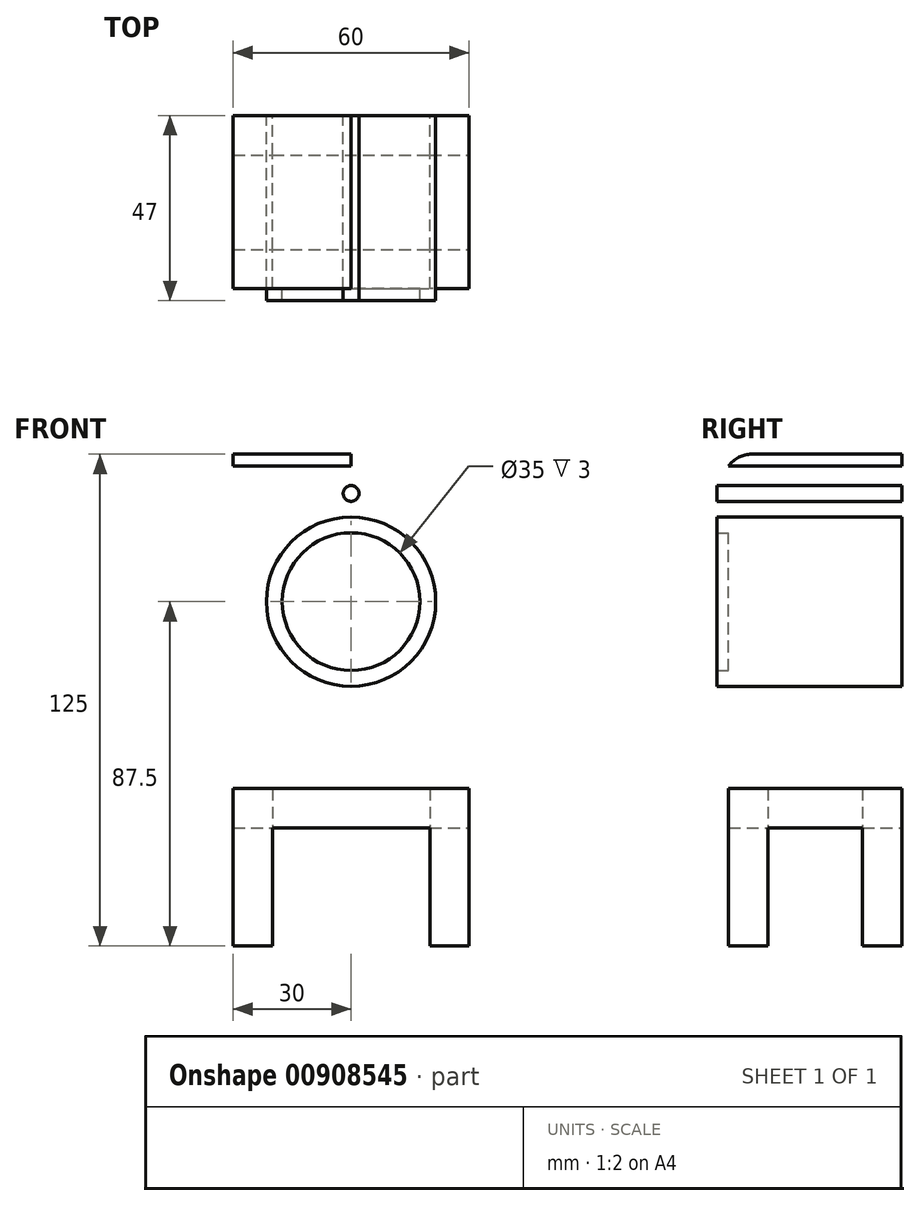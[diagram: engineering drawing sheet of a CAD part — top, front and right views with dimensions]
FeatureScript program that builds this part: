
annotation { "Feature Type Name" : "Feature", "Feature Type Description" : "" }
export const myFeature = defineFeature(function(context is Context, id is Id, definition is map)
    precondition{}
    {
        {
            var Q0;
            Q0=qCreatedBy(makeId("Front.planeOp"),FACE);
            var sketch = newSketch(context, id + "F0", { "sketchPlane" : qUnion([Q0])});
            skLineSegment(sketch, "E0.bottom", {"start": v(-30, 42.5) * mm, "end": v(30, 42.5) * mm});
            skLineSegment(sketch, "E0.top", {"start": v(-30, -42.5) * mm, "end": v(30, -42.5) * mm});
            skLineSegment(sketch, "E0.left", {"start": v(-30, 42.5) * mm, "end": v(-30, -42.5) * mm});
            skLineSegment(sketch, "E0.right", {"start": v(30, 42.5) * mm, "end": v(30, -42.5) * mm});
            skPoint(sketch, "E0.middle", {"position": v(0, 0) * mm});
            skPoint(sketch, "E1", {"position": v(0, 26.5) * mm});
            skPoint(sketch, "E1.positionSnap0", {"position": v(0, 42.5) * mm});
            skLineSegment(sketch, "E2", {"start": v(0, 42.5) * mm, "end": v(0, 26.5) * mm});
            skPoint(sketch, "E3", {"position": v(0, -16.5) * mm});
            skLineSegment(sketch, "E4", {"start": v(0, 26.5) * mm, "end": v(0, -16.5) * mm});
            skPoint(sketch, "E5", {"position": v(0, 5) * mm});
            skCircle(sketch, "E6", {"center": v(0, 5) * mm, "radius": 21.5 * mm});
            skCircle(sketch, "E7.0", {"center": v(0, 5) * mm, "radius": 17.5 * mm});
            skLineSegment(sketch, "E8.top", {"start": v(-30, 27.5) * mm, "end": v(30, 27.5) * mm});
            skLineSegment(sketch, "E8.left", {"start": v(-30, 42.5) * mm, "end": v(-30, 27.5) * mm});
            skLineSegment(sketch, "E8.right", {"start": v(30, 42.5) * mm, "end": v(30, 27.5) * mm});
            skLineSegment(sketch, "E9.top", {"start": v(-30, 39.5) * mm, "end": v(30, 39.5) * mm});
            skLineSegment(sketch, "E9.left", {"start": v(-30, 42.5) * mm, "end": v(-30, 39.5) * mm});
            skLineSegment(sketch, "E9.right", {"start": v(30, 42.5) * mm, "end": v(30, 39.5) * mm});
            skPoint(sketch, "E10", {"position": v(0, 32.5) * mm});
            skCircle(sketch, "E11", {"center": v(0, 32.5) * mm, "radius": 2 * mm});
            skLineSegment(sketch, "E12.bottom", {"start": v(-30, -42.5) * mm, "end": v(-20, -42.5) * mm});
            skLineSegment(sketch, "E12.top", {"start": v(-30, -82.5) * mm, "end": v(-20, -82.5) * mm});
            skLineSegment(sketch, "E12.left", {"start": v(-30, -42.5) * mm, "end": v(-30, -82.5) * mm});
            skLineSegment(sketch, "E12.right", {"start": v(-20, -42.5) * mm, "end": v(-20, -82.5) * mm});
            skLineSegment(sketch, "E13.bottom", {"start": v(30, -42.5) * mm, "end": v(20, -42.5) * mm});
            skLineSegment(sketch, "E13.top", {"start": v(30, -82.5) * mm, "end": v(20, -82.5) * mm});
            skLineSegment(sketch, "E13.left", {"start": v(30, -42.5) * mm, "end": v(30, -82.5) * mm});
            skLineSegment(sketch, "E13.right", {"start": v(20, -42.5) * mm, "end": v(20, -82.5) * mm});
            skLineSegment(sketch, "E14.top", {"start": v(-30, -52.5) * mm, "end": v(30, -52.5) * mm});
            skLineSegment(sketch, "E14.left", {"start": v(-30, -42.5) * mm, "end": v(-30, -52.5) * mm});
            skLineSegment(sketch, "E14.right", {"start": v(30, -42.5) * mm, "end": v(30, -52.5) * mm});
            skLineSegment(sketch, "E15.top", {"start": v(-30, -82.5) * mm, "end": v(30, -82.5) * mm});
            skSolve(sketch);
        }
        {
            var Q0;
            {var subQ0=sQuery(id+"F0.wireOp",EDGE,"E6");var subQ1=sQuery(id+"F0.wireOp",EDGE,"E4");var subQ2=makeQuery(id+"F0.imprint","INTERSECT",VERTEX,{"disambiguationData":[OD(0.0)],"derivedFrom":[subQ1,subQ0]});Q0=makeQuery(id+"F0.imprint","IMPRINT",FACE,{"disambiguationData":[TD([[makeQuery(id+"F0.imprint","IMPRINT",EDGE,{"disambiguationData":[TD([[subQ2,-1.0]])],"derivedFrom":subQ1}),-1.0]])]});}
            var Q1;
            {var subQ0=sQuery(id+"F0.wireOp",EDGE,"E6");var subQ1=sQuery(id+"F0.wireOp",EDGE,"E4");var subQ2=makeQuery(id+"F0.imprint","INTERSECT",VERTEX,{"disambiguationData":[OD(0.0)],"derivedFrom":[subQ1,subQ0]});Q1=makeQuery(id+"F0.imprint","IMPRINT",FACE,{"disambiguationData":[TD([[makeQuery(id+"F0.imprint","IMPRINT",EDGE,{"disambiguationData":[TD([[subQ2,-1.0]])],"derivedFrom":subQ1}),1.0]])]});}
            var Q2;
            {var subQ0=sQuery(id+"F0.wireOp",EDGE,"E8.left");Q2=makeQuery(id+"F0.imprint","IMPRINT",FACE,{"disambiguationData":[TD([[makeQuery(id+"F0.imprint","IMPRINT",EDGE,{"derivedFrom":subQ0}),1.0]])]});}
            var Q3;
            {var subQ0=sQuery(id+"F0.wireOp",EDGE,"E8.right");Q3=makeQuery(id+"F0.imprint","IMPRINT",FACE,{"disambiguationData":[TD([[makeQuery(id+"F0.imprint","IMPRINT",EDGE,{"derivedFrom":subQ0}),-1.0]])]});}
            var Q4;
            {var subQ5=sQuery(id+"F0.wireOp",EDGE,"E9.right");Q4=makeQuery(id+"F0.imprint","IMPRINT",FACE,{"disambiguationData":[TD([[makeQuery(id+"F0.imprint","IMPRINT",EDGE,{"derivedFrom":subQ5}),-1.0]])]});}
            var Q5;
            {var subQ5=sQuery(id+"F0.wireOp",EDGE,"E9.left");Q5=makeQuery(id+"F0.imprint","IMPRINT",FACE,{"disambiguationData":[TD([[makeQuery(id+"F0.imprint","IMPRINT",EDGE,{"derivedFrom":subQ5}),1.0]])]});}
            var Q6;
            {var subQ0=sQuery(id+"F0.wireOp",EDGE,"E7.0");var subQ1=sQuery(id+"F0.wireOp",EDGE,"E4");var subQ2=makeQuery(id+"F0.imprint","INTERSECT",VERTEX,{"disambiguationData":[OD(0.0)],"derivedFrom":[subQ1,subQ0]});Q6=makeQuery(id+"F0.imprint","IMPRINT",FACE,{"disambiguationData":[TD([[makeQuery(id+"F0.imprint","IMPRINT",EDGE,{"disambiguationData":[TD([[subQ2,-1.0]])],"derivedFrom":subQ1}),1.0]])]});}
            var Q7;
            {var subQ0=sQuery(id+"F0.wireOp",EDGE,"E7.0");var subQ1=sQuery(id+"F0.wireOp",EDGE,"E4");var subQ2=makeQuery(id+"F0.imprint","INTERSECT",VERTEX,{"disambiguationData":[OD(0.0)],"derivedFrom":[subQ1,subQ0]});Q7=makeQuery(id+"F0.imprint","IMPRINT",FACE,{"disambiguationData":[TD([[makeQuery(id+"F0.imprint","IMPRINT",EDGE,{"disambiguationData":[TD([[subQ2,-1.0]])],"derivedFrom":subQ1}),-1.0]])]});}
            var Q8;
            {var subQ7=sQuery(id+"F0.wireOp",EDGE,"E0.left");Q8=makeQuery(id+"F0.imprint","IMPRINT",FACE,{"disambiguationData":[TD([[makeQuery(id+"F0.imprint","IMPRINT",EDGE,{"derivedFrom":subQ7}),1.0]])]});}
            var Q9;
            {var subQ0=sQuery(id+"F0.wireOp",EDGE,"E15.top");var subQ1=sQuery(id+"F0.wireOp",EDGE,"E13.right");var subQ2=makeQuery(id+"F0.imprint","INTERSECT",VERTEX,{"derivedFrom":[subQ1,subQ0]});Q9=makeQuery(id+"F0.imprint","IMPRINT",FACE,{"disambiguationData":[TD([[makeQuery(id+"F0.imprint","IMPRINT",EDGE,{"disambiguationData":[TD([[subQ2,1.0]])],"derivedFrom":subQ1}),1.0]])]});}
            var Q10;
            {var subQ0=sQuery(id+"F0.wireOp",EDGE,"E0.top");var subQ1=sQuery(id+"F0.wireOp",EDGE,"E13.right");var subQ2=makeQuery(id+"F0.imprint","INTERSECT",VERTEX,{"derivedFrom":[subQ1,subQ0]});Q10=makeQuery(id+"F0.imprint","IMPRINT",FACE,{"disambiguationData":[TD([[makeQuery(id+"F0.imprint","IMPRINT",EDGE,{"disambiguationData":[TD([[subQ2,-1.0]])],"derivedFrom":subQ1}),1.0]])]});}
            var Q11;
            {var subQ0=sQuery(id+"F0.wireOp",EDGE,"E0.top");var subQ1=sQuery(id+"F0.wireOp",EDGE,"E12.right");var subQ2=makeQuery(id+"F0.imprint","INTERSECT",VERTEX,{"derivedFrom":[subQ1,subQ0]});Q11=makeQuery(id+"F0.imprint","IMPRINT",FACE,{"disambiguationData":[TD([[makeQuery(id+"F0.imprint","IMPRINT",EDGE,{"disambiguationData":[TD([[subQ2,-1.0]])],"derivedFrom":subQ1}),-1.0]])]});}
            var Q12;
            {var subQ0=sQuery(id+"F0.wireOp",EDGE,"E15.top");var subQ1=sQuery(id+"F0.wireOp",EDGE,"E12.right");var subQ2=makeQuery(id+"F0.imprint","INTERSECT",VERTEX,{"derivedFrom":[subQ1,subQ0]});Q12=makeQuery(id+"F0.imprint","IMPRINT",FACE,{"disambiguationData":[TD([[makeQuery(id+"F0.imprint","IMPRINT",EDGE,{"disambiguationData":[TD([[subQ2,1.0]])],"derivedFrom":subQ1}),-1.0]])]});}
            var Q13;
            {var subQ0=sQuery(id+"F0.wireOp",EDGE,"E0.top");var subQ1=sQuery(id+"F0.wireOp",EDGE,"E12.right");var subQ2=makeQuery(id+"F0.imprint","INTERSECT",VERTEX,{"derivedFrom":[subQ1,subQ0]});Q13=makeQuery(id+"F0.imprint","IMPRINT",FACE,{"disambiguationData":[TD([[makeQuery(id+"F0.imprint","IMPRINT",EDGE,{"disambiguationData":[TD([[subQ2,-1.0]])],"derivedFrom":subQ1}),1.0]])]});}
            extrude(context, id + "F1", {"entities" : qUnion([Q0, Q1, Q2, Q3, Q4, Q5, Q6, Q7, Q8, Q9, Q10, Q11, Q12, Q13]), "depth" : 44 * mm, "offsetDistance" : 25 * mm});
        }
        {
            var Q0;
            {var subQ0=sQuery(id+"F0.wireOp",EDGE,"E6");var subQ1=sQuery(id+"F0.wireOp",EDGE,"E4");var subQ2=makeQuery(id+"F0.imprint","INTERSECT",VERTEX,{"disambiguationData":[OD(0.0)],"derivedFrom":[subQ1,subQ0]});Q0=makeQuery(id+"F0.imprint","IMPRINT",FACE,{"disambiguationData":[TD([[makeQuery(id+"F0.imprint","IMPRINT",EDGE,{"disambiguationData":[TD([[subQ2,-1.0]])],"derivedFrom":subQ1}),1.0]])]});}
            var Q1;
            {var subQ0=sQuery(id+"F0.wireOp",EDGE,"E6");var subQ1=sQuery(id+"F0.wireOp",EDGE,"E4");var subQ2=makeQuery(id+"F0.imprint","INTERSECT",VERTEX,{"disambiguationData":[OD(0.0)],"derivedFrom":[subQ1,subQ0]});Q1=makeQuery(id+"F0.imprint","IMPRINT",FACE,{"disambiguationData":[TD([[makeQuery(id+"F0.imprint","IMPRINT",EDGE,{"disambiguationData":[TD([[subQ2,-1.0]])],"derivedFrom":subQ1}),-1.0]])]});}
            var Q2;
            {var subQ0=sQuery(id+"F0.wireOp",EDGE,"zrFD8z1w-E58j-qKlx-5lVt-mCnEbS1Ubnud");var subQ1=sQuery(id+"F0.wireOp",EDGE,"E2");var subQ2=makeQuery(id+"F0.imprint","INTERSECT",VERTEX,{"disambiguationData":[OD(0.0)],"derivedFrom":[subQ1,subQ0]});Q2=makeQuery(id+"F0.imprint","IMPRINT",FACE,{"disambiguationData":[TD([[makeQuery(id+"F0.imprint","IMPRINT",EDGE,{"disambiguationData":[TD([[subQ2,-1.0]])],"derivedFrom":subQ1}),1.0]])]});}
            var Q3;
            {var subQ0=sQuery(id+"F0.wireOp",EDGE,"zrFD8z1w-E58j-qKlx-5lVt-mCnEbS1Ubnud");var subQ1=sQuery(id+"F0.wireOp",EDGE,"E2");var subQ2=makeQuery(id+"F0.imprint","INTERSECT",VERTEX,{"disambiguationData":[OD(0.0)],"derivedFrom":[subQ1,subQ0]});Q3=makeQuery(id+"F0.imprint","IMPRINT",FACE,{"disambiguationData":[TD([[makeQuery(id+"F0.imprint","IMPRINT",EDGE,{"disambiguationData":[TD([[subQ2,-1.0]])],"derivedFrom":subQ1}),-1.0]])]});}
            extrude(context, id + "F2", {"entities" : qUnion([Q0, Q1, Q2, Q3]), "operationType" : NewBodyOperationType.ADD, "depth" : 47 * mm, "offsetDistance" : 25 * mm});
        }
        {
            var Q0;
            Q0=makeQuery(id+"F1.opExtrude","CAP_EDGE",EDGE,{"disambiguationData":[OSD([sQuery(id+"F0.wireOp",EDGE,"E0.bottom")])],"isStart":false});
            fillet(context, id + "F3", {"entities" : qUnion([Q0]), "radius" : 7.24 * mm, "tangentPropagation" : true, "allowEdgeOverflow" : false});
        }
        {
            var Q0;
            {var subQ0=sQuery(id+"F0.wireOp",EDGE,"E15.top");var subQ1=sQuery(id+"F0.wireOp",EDGE,"E12.right");var subQ2=makeQuery(id+"F0.imprint","INTERSECT",VERTEX,{"derivedFrom":[subQ1,subQ0]});Q0=makeQuery(id+"F0.imprint","IMPRINT",FACE,{"disambiguationData":[TD([[makeQuery(id+"F0.imprint","IMPRINT",EDGE,{"disambiguationData":[TD([[subQ2,1.0]])],"derivedFrom":subQ1}),1.0]])]});}
            var Q1;
            {var subQ0=sQuery(id+"F0.wireOp",EDGE,"E15.top");var subQ1=sQuery(id+"F0.wireOp",EDGE,"E13.right");var subQ2=makeQuery(id+"F0.imprint","INTERSECT",VERTEX,{"derivedFrom":[subQ1,subQ0]});Q1=makeQuery(id+"F0.imprint","IMPRINT",FACE,{"disambiguationData":[TD([[makeQuery(id+"F0.imprint","IMPRINT",EDGE,{"disambiguationData":[TD([[subQ2,1.0]])],"derivedFrom":subQ1}),1.0]])]});}
            var Q2;
            {var subQ0=sQuery(id+"F0.wireOp",EDGE,"E15.top");var subQ1=sQuery(id+"F0.wireOp",EDGE,"E12.right");var subQ2=makeQuery(id+"F0.imprint","INTERSECT",VERTEX,{"derivedFrom":[subQ1,subQ0]});Q2=makeQuery(id+"F0.imprint","IMPRINT",FACE,{"disambiguationData":[TD([[makeQuery(id+"F0.imprint","IMPRINT",EDGE,{"disambiguationData":[TD([[subQ2,1.0]])],"derivedFrom":subQ1}),-1.0]])]});}
            var Q3;
            {var subQ0=sQuery(id+"F0.wireOp",EDGE,"E0.top");var subQ1=sQuery(id+"F0.wireOp",EDGE,"E12.right");var subQ2=makeQuery(id+"F0.imprint","INTERSECT",VERTEX,{"derivedFrom":[subQ1,subQ0]});Q3=makeQuery(id+"F0.imprint","IMPRINT",FACE,{"disambiguationData":[TD([[makeQuery(id+"F0.imprint","IMPRINT",EDGE,{"disambiguationData":[TD([[subQ2,-1.0]])],"derivedFrom":subQ1}),1.0]])]});}
            var Q4;
            {var subQ0=sQuery(id+"F0.wireOp",EDGE,"E12.top");var subQ1=sQuery(id+"F0.wireOp",EDGE,"E0.bottom");var subQ2=sQuery(id+"F0.wireOp",EDGE,"E14.right");var subQ3=sQuery(id+"F0.wireOp",EDGE,"E13.left");var subQ4=sQuery(id+"F0.wireOp",EDGE,"E9.right");var subQ5=sQuery(id+"F0.wireOp",EDGE,"E8.right");var subQ6=sQuery(id+"F0.wireOp",EDGE,"E0.right");var subQ7=sQuery(id+"F0.wireOp",EDGE,"E14.left");var subQ8=sQuery(id+"F0.wireOp",EDGE,"E12.left");var subQ9=sQuery(id+"F0.wireOp",EDGE,"E9.left");var subQ10=sQuery(id+"F0.wireOp",EDGE,"E8.left");var subQ11=sQuery(id+"F0.wireOp",EDGE,"E0.left");var subQ12=sQuery(id+"F0.wireOp",EDGE,"E12.right");var subQ13=sQuery(id+"F0.wireOp",EDGE,"E13.top");var subQ14=sQuery(id+"F0.wireOp",EDGE,"E11");var subQ15=sQuery(id+"F0.wireOp",EDGE,"E13.right");var subQ16=sQuery(id+"F0.wireOp",EDGE,"E0.top");Q4=makeQuery(id+"F2.boolean.opBoolean","SPLIT",FACE,{"disambiguationData":[TD([makeQuery(id+"F1.opExtrude","SWEPT_FACE",FACE,{"disambiguationData":[OSD([subQ1])]})])],"derivedFrom":makeQuery(id+"F1.opExtrude","CAP_FACE",FACE,{"disambiguationData":[OSD([subQ11,subQ6,subQ10,subQ5,subQ1,subQ9,subQ4,subQ14,subQ0,subQ8,subQ12,subQ13,subQ3,subQ15,subQ16,subQ7,subQ2])],"isStart":false})});}
            extrude(context, id + "F4", {"entities" : qUnion([Q0, Q1, Q2, Q3]), "operationType" : NewBodyOperationType.REMOVE, "endBound" : BoundingType.UP_TO_SURFACE, "depth" : 14.7 * mm, "endBoundEntityFace" : qUnion([Q4]), "hasOffset" : true, "offsetDistance" : 10 * mm, "hasSecondDirection" : true, "secondDirectionOppositeDirection" : false, "secondDirectionDepth" : 10 * mm});
        }
        {
            var Q0;
            {var subQ0=sQuery(id+"F0.wireOp",EDGE,"E15.top");var subQ1=sQuery(id+"F0.wireOp",EDGE,"E12.right");var subQ2=makeQuery(id+"F0.imprint","INTERSECT",VERTEX,{"derivedFrom":[subQ1,subQ0]});Q0=makeQuery(id+"F0.imprint","IMPRINT",FACE,{"disambiguationData":[TD([[makeQuery(id+"F0.imprint","IMPRINT",EDGE,{"disambiguationData":[TD([[subQ2,1.0]])],"derivedFrom":subQ1}),1.0]])]});}
            extrude(context, id + "F5", {"entities" : qUnion([Q0]), "operationType" : NewBodyOperationType.REMOVE, "depth" : 50 * mm, "offsetDistance" : 25 * mm});
        }
    });
